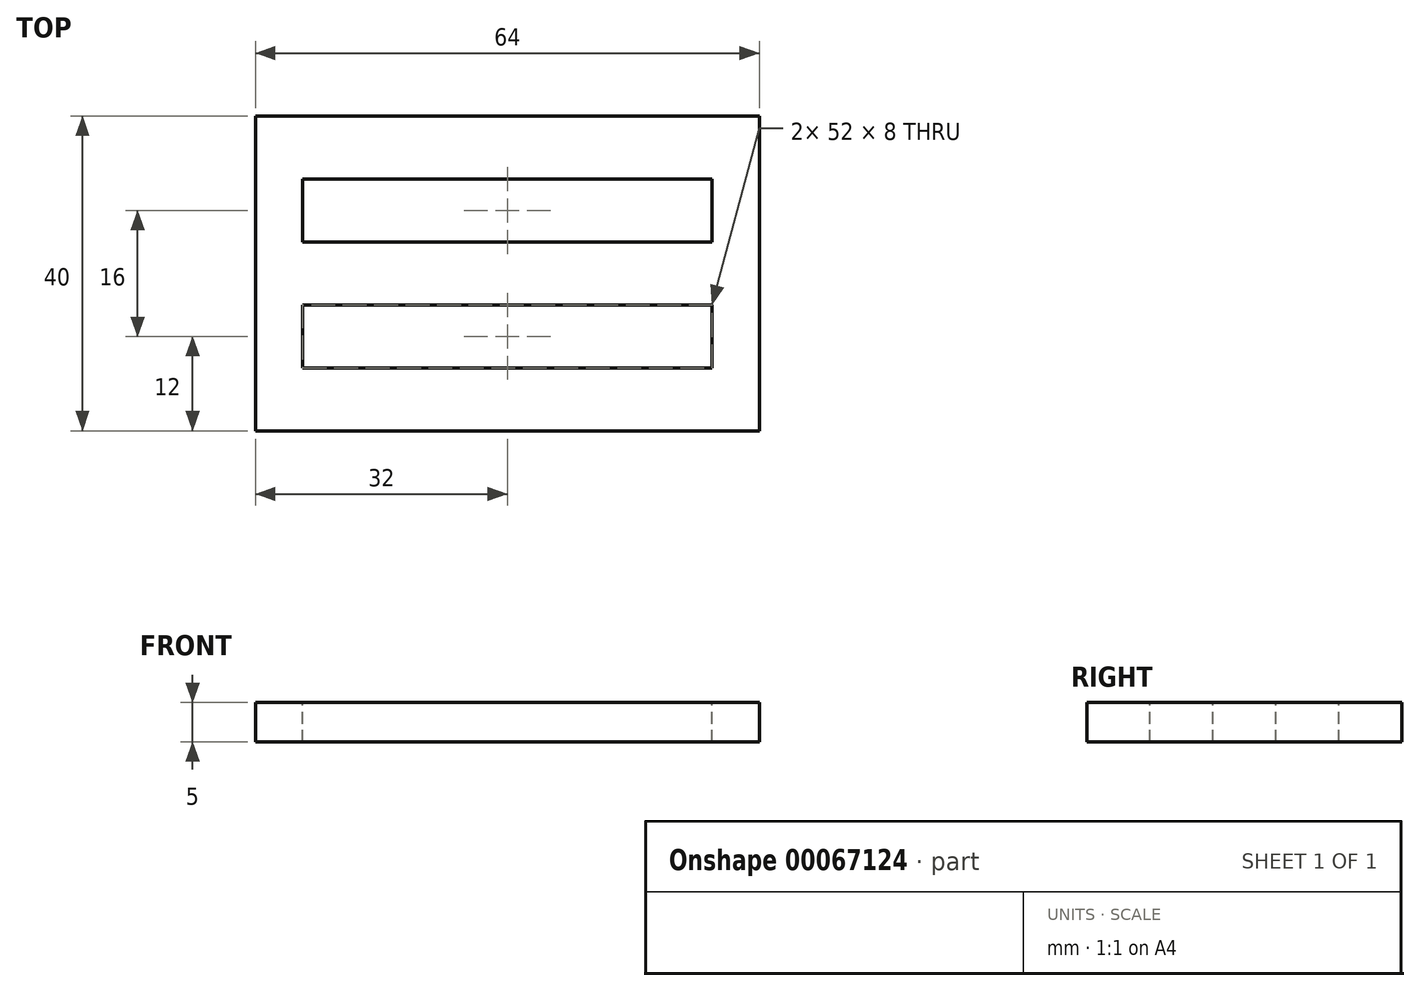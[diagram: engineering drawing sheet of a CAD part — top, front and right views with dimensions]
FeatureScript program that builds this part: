
annotation { "Feature Type Name" : "Feature", "Feature Type Description" : "" }
export const myFeature = defineFeature(function(context is Context, id is Id, definition is map)
    precondition{}
    {
        {
            var Q0;
            Q0=qCreatedBy(makeId("Top.planeOp"),FACE);
            var sketch = newSketch(context, id + "F0", { "sketchPlane" : qUnion([Q0])});
            skLineSegment(sketch, "E0.bottom", {"start": v(0, 0) * mm, "end": v(64, 0) * mm});
            skLineSegment(sketch, "E0.top", {"start": v(0, 40) * mm, "end": v(64, 40) * mm});
            skLineSegment(sketch, "E0.left", {"start": v(0, 0) * mm, "end": v(0, 40) * mm});
            skLineSegment(sketch, "E0.right", {"start": v(64, 0) * mm, "end": v(64, 40) * mm});
            skSolve(sketch);
        }
        {
            var Q0;
            Q0 = qSketchRegion(id + "F0", true);
            extrude(context, id + "F1", {"entities" : qUnion([Q0]), "depth" : 5 * mm});
        }
        {
            var Q0;
            Q0=makeQuery(id+"F1.opExtrude","CAP_FACE",FACE,{"disambiguationData":[OSD([sQuery(id+"F0.wireOp",EDGE,"E0.bottom"),sQuery(id+"F0.wireOp",EDGE,"E0.top"),sQuery(id+"F0.wireOp",EDGE,"E0.left"),sQuery(id+"F0.wireOp",EDGE,"E0.right")])],"isStart":false});
            var sketch = newSketch(context, id + "F2", { "sketchPlane" : qUnion([Q0])});
            skLineSegment(sketch, "E1.bottom", {"start": v(6, 32) * mm, "end": v(58, 32) * mm});
            skLineSegment(sketch, "E1.top", {"start": v(6, 24) * mm, "end": v(58, 24) * mm});
            skLineSegment(sketch, "E1.left", {"start": v(6, 32) * mm, "end": v(6, 24) * mm});
            skLineSegment(sketch, "E1.right", {"start": v(58, 32) * mm, "end": v(58, 24) * mm});
            skLineSegment(sketch, "E2.1.0.0", {"start": v(6, 16) * mm, "end": v(58, 16) * mm});
            skLineSegment(sketch, "E2.1.0.1", {"start": v(6, 16) * mm, "end": v(6, 8) * mm});
            skLineSegment(sketch, "E2.1.0.2", {"start": v(6, 8) * mm, "end": v(58, 8) * mm});
            skLineSegment(sketch, "E2.1.0.3", {"start": v(58, 16) * mm, "end": v(58, 8) * mm});
            skLineSegment(sketch, "E2.direction1", {"start": v(6, 32) * mm, "end": v(6, 16) * mm, "construction": true});
            skSolve(sketch);
        }
        {
            var Q0;
            Q0 = qSketchRegion(id + "F2", true);
            extrude(context, id + "F3", {"entities" : qUnion([Q0]), "operationType" : NewBodyOperationType.REMOVE, "endBound" : BoundingType.THROUGH_ALL, "oppositeDirection" : true, "depth" : 25 * mm});
        }
    });
